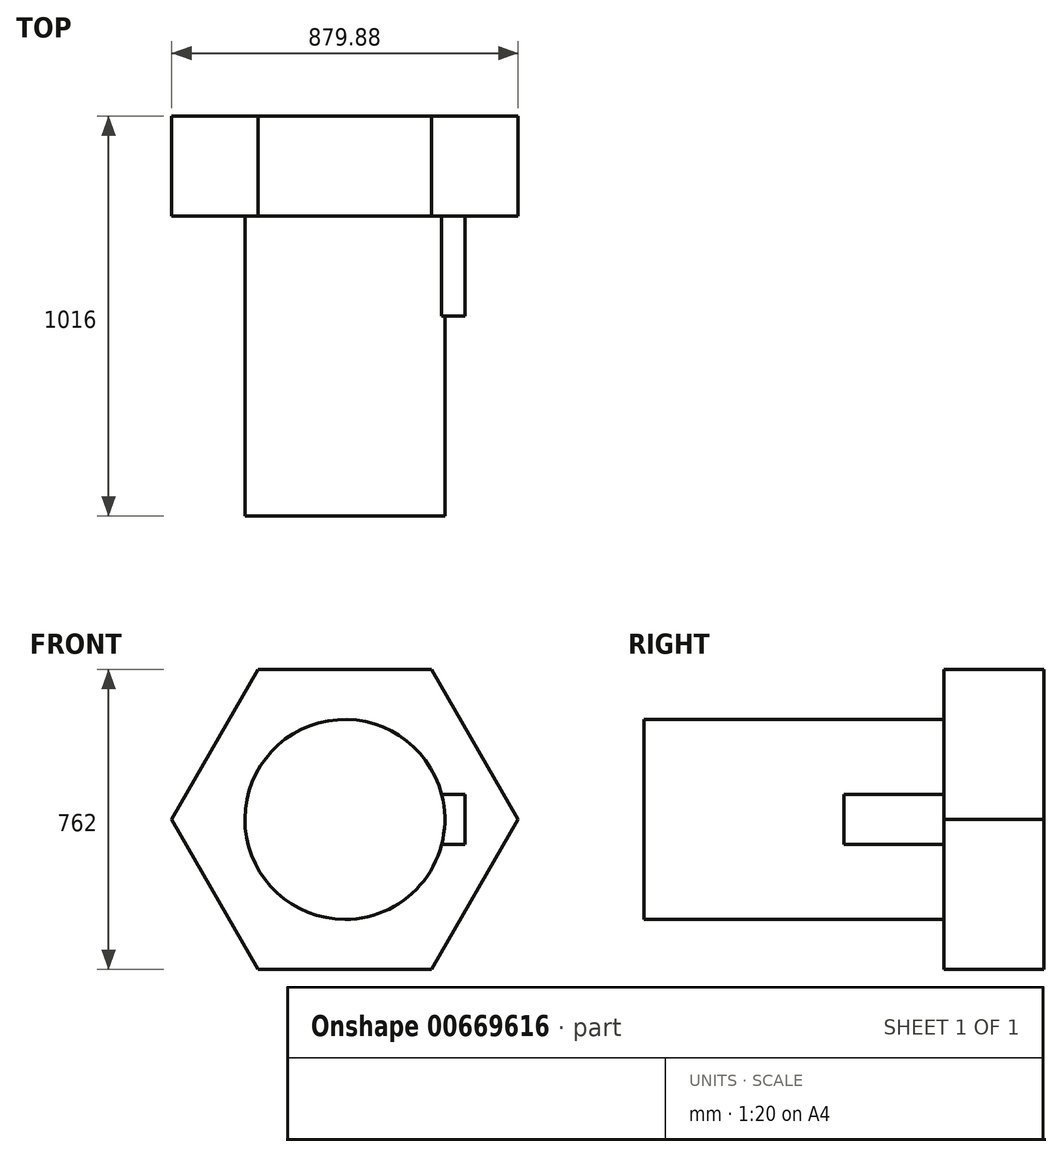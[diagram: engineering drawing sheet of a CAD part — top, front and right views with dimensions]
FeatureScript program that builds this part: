
annotation { "Feature Type Name" : "Feature", "Feature Type Description" : "" }
export const myFeature = defineFeature(function(context is Context, id is Id, definition is map)
    precondition{}
    {
        {
            var Q0;
            Q0=qCreatedBy(makeId("Front.planeOp"),FACE);
            var sketch = newSketch(context, id + "F0", { "sketchPlane" : qUnion([Q0])});
            skCircle(sketch, "E0.cCircle", {"center": v(0, 0) * mm, "radius": 381 * mm, "construction": true});
            skLineSegment(sketch, "E0.0", {"start": v(-219.97, 381) * mm, "end": v(219.97, 381) * mm});
            skLineSegment(sketch, "E0.1", {"start": v(219.97, 381) * mm, "end": v(439.94, 0) * mm});
            skLineSegment(sketch, "E0.2", {"start": v(439.94, 0) * mm, "end": v(219.97, -381) * mm});
            skLineSegment(sketch, "E0.3", {"start": v(219.97, -381) * mm, "end": v(-219.97, -381) * mm});
            skLineSegment(sketch, "E0.4", {"start": v(-219.97, -381) * mm, "end": v(-439.94, 0) * mm});
            skLineSegment(sketch, "E0.5", {"start": v(-439.94, 0) * mm, "end": v(-219.97, 381) * mm});
            skPoint(sketch, "E0.0.midPoint", {"position": v(0, 381) * mm});
            skArc(sketch, "E1", {"start": v(245.93, 63.5) * mm, "mid": v(-254, 0) * mm, "end": v(245.93, -63.5) * mm});
            skLineSegment(sketch, "E2.bottom", {"start": v(304.8, 63.5) * mm, "end": v(245.93, 63.5) * mm});
            skLineSegment(sketch, "E2.top", {"start": v(304.8, -63.5) * mm, "end": v(245.93, -63.5) * mm});
            skLineSegment(sketch, "E2.left", {"start": v(304.8, 63.5) * mm, "end": v(304.8, -63.5) * mm});
            skPoint(sketch, "E2.middle", {"position": v(254, 0) * mm});
            skPoint(sketch, "E2.right.start.orphan", {"position": v(203.2, 63.5) * mm});
            skPoint(sketch, "E3.orphan", {"position": v(203.2, -63.5) * mm});
            skCircle(sketch, "E4", {"center": v(0, 0) * mm, "radius": 254 * mm});
            skSolve(sketch);
        }
        {
            var Q0;
            {var subQ0=sQuery(id+"F0.wireOp",EDGE,"E4");var subQ1=makeQuery(id+"F0.imprint","INTERSECT",VERTEX,{"derivedFrom":[sQuery(id+"F0.wireOp",EDGE,"E2.bottom"),subQ0]});Q0=makeQuery(id+"F0.imprint","IMPRINT",FACE,{"disambiguationData":[TD([[makeQuery(id+"F0.imprint","IMPRINT",EDGE,{"disambiguationData":[TD([[subQ1,-1.0]])],"derivedFrom":subQ0}),1.0]])]});}
            extrude(context, id + "F1", {"entities" : qUnion([Q0]), "depth" : 762 * mm, "offsetDistance" : 25.4 * mm});
        }
        {
            var Q0;
            {var subQ0=sQuery(id+"F0.wireOp",EDGE,"E2.bottom");Q0=makeQuery(id+"F0.imprint","IMPRINT",FACE,{"disambiguationData":[TD([[makeQuery(id+"F0.imprint","IMPRINT",EDGE,{"derivedFrom":subQ0}),1.0]])]});}
            extrude(context, id + "F2", {"entities" : qUnion([Q0]), "operationType" : NewBodyOperationType.ADD, "depth" : 254 * mm, "offsetDistance" : 25.4 * mm});
        }
        {
            var Q0;
            {var subQ0=sQuery(id+"F0.wireOp",EDGE,"E4");var subQ1=makeQuery(id+"F0.imprint","INTERSECT",VERTEX,{"derivedFrom":[sQuery(id+"F0.wireOp",EDGE,"E2.bottom"),subQ0]});Q0=makeQuery(id+"F0.imprint","IMPRINT",FACE,{"disambiguationData":[TD([[makeQuery(id+"F0.imprint","IMPRINT",EDGE,{"disambiguationData":[TD([[subQ1,-1.0]])],"derivedFrom":subQ0}),1.0]])]});}
            var sketch = newSketch(context, id + "F3", { "sketchPlane" : qUnion([Q0])});
            skCircle(sketch, "E5.cCircle", {"center": v(0, 0) * mm, "radius": 381 * mm, "construction": true});
            skLineSegment(sketch, "E5.0", {"start": v(-219.97, 381) * mm, "end": v(219.97, 381) * mm});
            skLineSegment(sketch, "E5.1", {"start": v(219.97, 381) * mm, "end": v(439.94, 0) * mm});
            skLineSegment(sketch, "E5.2", {"start": v(439.94, 0) * mm, "end": v(219.97, -381) * mm});
            skLineSegment(sketch, "E5.3", {"start": v(219.97, -381) * mm, "end": v(-219.97, -381) * mm});
            skLineSegment(sketch, "E5.4", {"start": v(-219.97, -381) * mm, "end": v(-439.94, 0) * mm});
            skLineSegment(sketch, "E5.5", {"start": v(-439.94, 0) * mm, "end": v(-219.97, 381) * mm});
            skPoint(sketch, "E5.0.midPoint", {"position": v(0, 381) * mm});
            skSolve(sketch);
        }
        {
            var Q0;
            Q0 = qSketchRegion(id + "F3", true);
            var Q1;
            Q1=makeQuery(id+"F0.imprint","IMPRINT",FACE,{"disambiguationData":[TD([[makeQuery(id+"F0.imprint","IMPRINT",EDGE,{"derivedFrom":sQuery(id+"F0.wireOp",EDGE,"E0.0")}),-1.0]])]});
            extrude(context, id + "F4", {"entities" : qUnion([Q0, Q1]), "operationType" : NewBodyOperationType.ADD, "oppositeDirection" : true, "depth" : 254 * mm, "offsetDistance" : 25.4 * mm});
        }
    });
